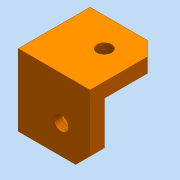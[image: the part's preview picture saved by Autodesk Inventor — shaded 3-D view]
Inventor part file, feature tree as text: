
AUTODESK INVENTOR PART (.ipt)
format: ipt  version: 2016 (Build 200138000, 138)  size: 164,864 bytes
history: native  units: mm
features: extrude x5, sketch x5, hole x3, chamfer x3
ambient origin geometry x8: Origin, YZ Plane, XZ Plane, XY Plane, X Axis, Y Axis, Z Axis, Center Point
bodies: Solid1 (feature_tree)
feature tree (16):
  extrude  "Extrusion1"  Depth=20.0mm
  extrude  "Extrusion2"  Depth=16.0mm TaperAngle=0.0deg
  hole  "Hole2"  [1 undecoded]
  hole  "Hole3"  [1 undecoded]
  hole  "Hole4"  [1 undecoded]
  chamfer  "Chamfer1"  Distance=7.0mm
  chamfer  "Chamfer2"  Distance=7.0mm
  chamfer  "Chamfer3"  Distance=7.0mm
  sketch  "Sketch3"  dims[d15=8.0mm d16=8.0mm d17=4.0mm d18=6.0mm d19=8.0mm d20=2.0mm d21=90.0deg d22=8.0mm d23=20.594885mm]
  sketch  "Sketch4"  dims[d24=8.0mm d25=8.0mm d26=4.0mm d27=6.0mm d28=8.0mm d29=2.0mm d30=90.0deg d31=8.0mm d32=20.594885mm]
  sketch  "Sketch5"  dims[d33=8.0mm d34=8.0mm d35=4.0mm d36=6.0mm d37=8.0mm d38=2.0mm d39=90.0deg d40=8.0mm d41=20.594885mm d42=4.0mm d43=2.0mm d44=45.0deg d45=4.0mm d46=2.0mm d47=45.0deg d48=4.0mm d49=2.0mm d50=45.0deg d51=7.0mm d52=7.0mm d53=7.0mm d54=2.0mm d55=0.0mm d56=2.0mm d57=0.0mm d58=2.0mm d59=0.0mm]
  extrude  "Extrusion3"  Depth=2.0mm TaperAngle=0.0deg
  extrude  "Extrusion4"  Depth=2.0mm TaperAngle=0.0deg
  extrude  "Extrusion5"  Depth=2.0mm TaperAngle=0.0deg
  sketch  "Sketch1"  dims[d0=20.0mm d1=20.0mm]
  sketch  "Sketch2"  dims[d2=4.0mm d3=0.0mm d4=16.0mm d5=0.0mm]
note: 3 required parameter values undecoded (feature->parameter linkage not recoverable at this tier; creation-order binding heuristic only, values carry confidence <= 0.55)
